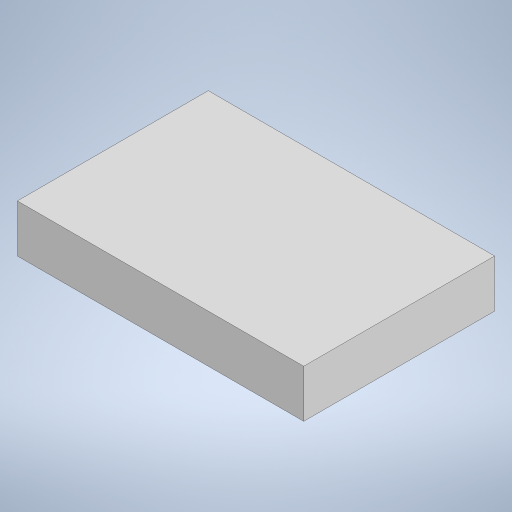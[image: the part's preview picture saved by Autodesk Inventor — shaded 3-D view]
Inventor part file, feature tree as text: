
AUTODESK INVENTOR PART (.ipt)
format: ipt  version: 2023 (Build 270158000, 158)  size: 188,928 bytes
history: native  units: mm
features: other x1, extrude x1, sketch x1
ambient origin geometry x8: Origin, YZ Plane, XZ Plane, XY Plane, X Axis, Y Axis, Z Axis, Center Point
bodies: Body1 (feature_tree)
feature tree (3):
  other  "Bryła1"
  extrude  "Wyciągnięcie proste1"  Depth=30.0mm
  sketch  "Szkic1"
